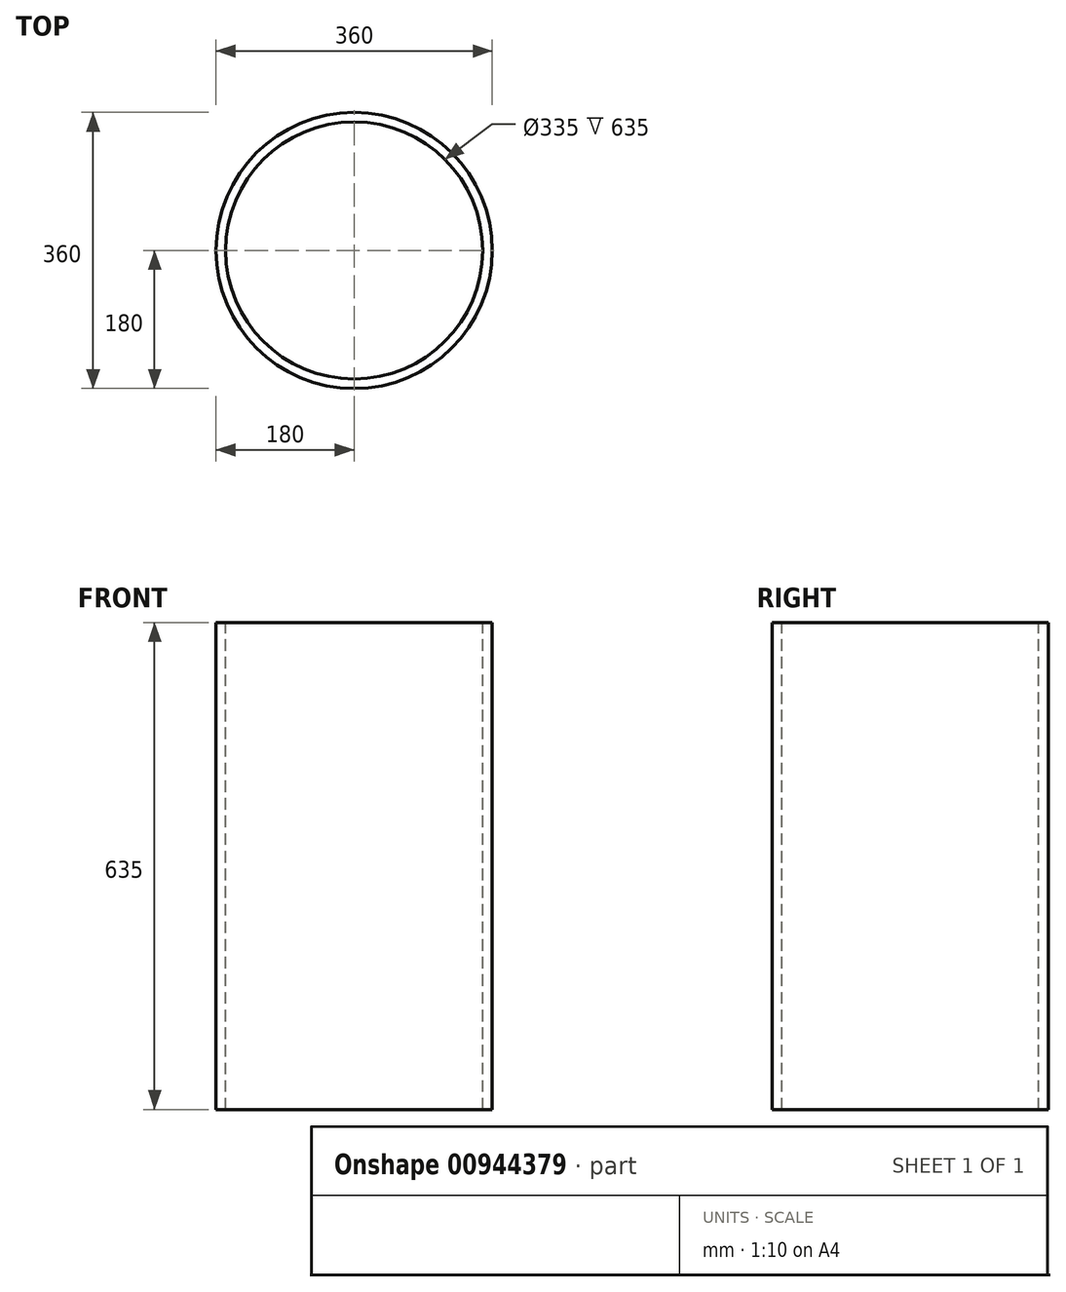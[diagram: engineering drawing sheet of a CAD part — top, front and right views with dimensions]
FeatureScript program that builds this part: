
annotation { "Feature Type Name" : "Feature", "Feature Type Description" : "" }
export const myFeature = defineFeature(function(context is Context, id is Id, definition is map)
    precondition{}
    {
        {
            var Q0;
            Q0=qCreatedBy(makeId("Top.planeOp"),FACE);
            var sketch = newSketch(context, id + "F0", { "sketchPlane" : qUnion([Q0])});
            skCircle(sketch, "E0", {"center": v(0, 0) * mm, "radius": 180 * mm});
            skCircle(sketch, "E1", {"center": v(0, 0) * mm, "radius": 167.5 * mm});
            skSolve(sketch);
        }
        {
            var Q0;
            Q0=makeQuery(id+"F0.imprint","IMPRINT",FACE,{"disambiguationData":[TD([[makeQuery(id+"F0.imprint","IMPRINT",EDGE,{"derivedFrom":sQuery(id+"F0.wireOp",EDGE,"E0")}),1.0]])]});
            extrude(context, id + "F1", {"entities" : qUnion([Q0]), "oppositeDirection" : true, "depth" : 635 * mm, "offsetDistance" : 25 * mm});
        }
    });
